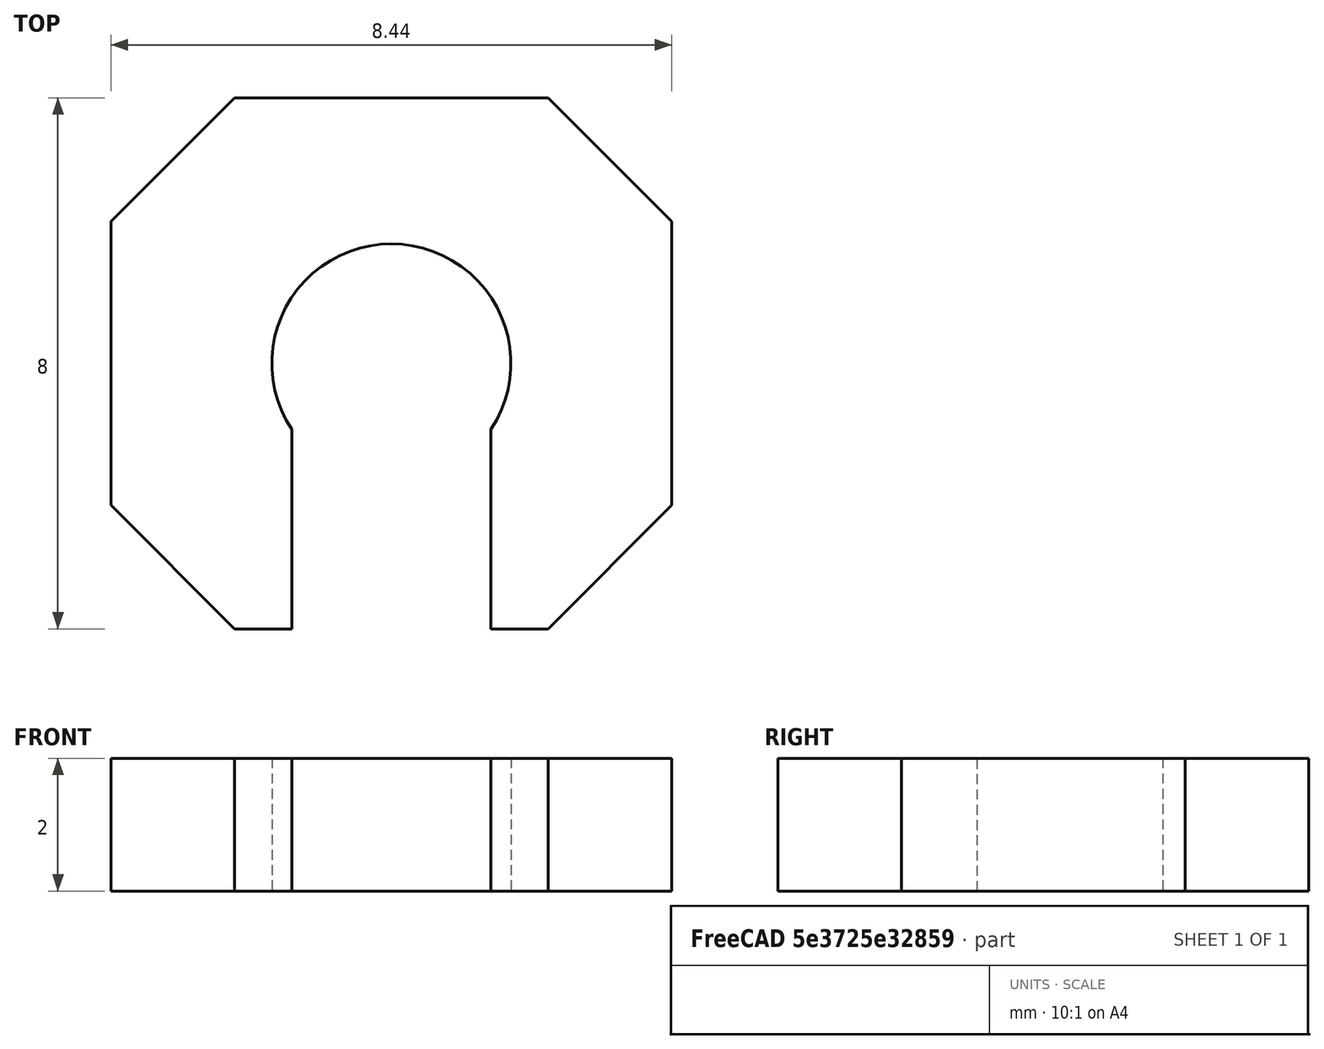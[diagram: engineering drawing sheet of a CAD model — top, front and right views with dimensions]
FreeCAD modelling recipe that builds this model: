
FCSTD DOCUMENT  (FreeCAD 0.17R13541 (Git))
Label: buteeSoupape
License: All rights reserved
LicenseURL: http://en.wikipedia.org/wiki/All_rights_reserved
objects: Sketcher::SketchObject×1, PartDesign::Pad×1, PartDesign::Body×1
note: 4 computed .brp shape members not serialized (recipe doc carries the construction recipe); baked Part::Feature solids carry a one-line shape summary decoded from their .brp

FEATURE [Sketcher::SketchObject] Sketch
  MapMode = 5
  Support = -> [XY_Plane]
  sketch-geometry (13):
    g0: LineSegment StartX=-2.3609 StartY=4 StartZ=0 EndX=2.3609 EndY=4 EndZ=0
    g1: LineSegment StartX=4.22367 StartY=2.13723 StartZ=0 EndX=4.22367 EndY=-2.13723 EndZ=0
    g2: LineSegment StartX=2.3609 StartY=-4 StartZ=0 EndX=1.5 EndY=-4 EndZ=0
    g3: LineSegment StartX=-4.22367 StartY=-2.13723 StartZ=0 EndX=-4.22367 EndY=2.13723 EndZ=0
    g4: ArcOfCircle CenterX=0 CenterY=0 CenterZ=0 NormalX=0 NormalY=0 NormalZ=1 AngleXU=0 Radius=1.8 StartAngle=5.6975 EndAngle=10.0105
    g5: LineSegment StartX=-1.5 StartY=-0.994987 StartZ=0 EndX=-1.5 EndY=-4 EndZ=0
    g6: LineSegment StartX=1.5 StartY=-0.994987 StartZ=0 EndX=1.5 EndY=-4 EndZ=0
    g7: LineSegment StartX=-1.5 StartY=-4 StartZ=0 EndX=-2.3609 EndY=-4 EndZ=0
    g8: LineSegment StartX=-4.22367 StartY=2.13723 StartZ=0 EndX=-2.3609 EndY=4 EndZ=0
    g9: LineSegment StartX=2.3609 StartY=4 StartZ=0 EndX=4.22367 EndY=2.13723 EndZ=0
    g10: LineSegment [constr] StartX=-5.83231 StartY=2.13723 StartZ=0 EndX=6.38011 EndY=2.13723 EndZ=0
    g11: LineSegment StartX=-4.22367 StartY=-2.13723 StartZ=0 EndX=-2.3609 EndY=-4 EndZ=0
    g12: LineSegment StartX=2.3609 StartY=-4 StartZ=0 EndX=4.22367 EndY=-2.13723 EndZ=0
  constraints (30):
    c: Horizontal(g0)
    c: Horizontal(g2)
    c: Vertical(g1)
    c: Vertical(g3)
    c: Coincident(g4,g-1)
    c: Radius(g4) = 1.8
    c: Vertical(g5)
    c: Vertical(g6)
    c: DistanceX(g5,g6) = 3
    c: Symmetric(g5,g6,g-2)
    c: Coincident(g4,g6)
    c: Coincident(g4,g5)
    c: PointOnObject(g2,g6)
    c: PointOnObject(g7,g5)
    c: Tangent(g2,g7)
    c: Coincident(g5,g7)
    c: Angle(g8,g0) = 2.35619
    c: Coincident(g0,g8)
    c: Coincident(g3,g8)
    c: Angle(g0,g9) = 2.35619
    c: Coincident(g0,g9)
    c: Coincident(g1,g9)
    c: Horizontal(g10)
    c: PointOnObject(g3,g10)
    c: PointOnObject(g1,g10)
    c: Coincident(g3,g11)
    c: Coincident(g7,g11)
    c: Coincident(g2,g12)
    c: Coincident(g1,g12)
    c: DistanceY(g2,g0) = 8
FEATURE [PartDesign::Pad] Pad
  Length = 2
  Length2 = 100
  Profile = -> Sketch
  Type = 0
FEATURE [PartDesign::Body] Body
  Group = -> [Sketch,Pad]
  Origin = -> Origin
  Tip = -> Pad
